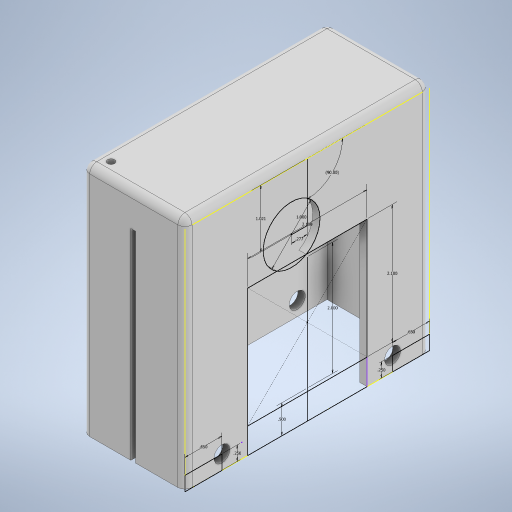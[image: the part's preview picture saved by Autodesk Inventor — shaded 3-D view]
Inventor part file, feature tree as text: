
AUTODESK INVENTOR PART (.ipt)
format: ipt  version: 2024.1 (Build 281209000, 209)  size: 335,872 bytes
history: native  units: in
note: dims shown in document units (in); Inventor stores cm internally (conversion verified against a paired STEP export)
features: extrude x6, sketch x6, hole x2, fillet x1
ambient origin geometry x8: Origin, YZ Plane, XZ Plane, XY Plane, X Axis, Y Axis, Z Axis, Center Point
bodies: Solid1 (feature_tree)
feature tree (15):
  extrude  "Extrusion1"  Depth=4.0in
  sketch  "Sketch2"  dims[d2=0.25in d3=0.25in]
  extrude  "Extrusion2"  Depth=0.25in
  hole  "Hole1"  [1 undecoded]
  extrude  "Extrusion3"  Depth=4.3in
  fillet  "Fillet1"  Radius=4.0in
  extrude  "Extrusion4"  Depth=0.25in
  hole  "Hole2"  [1 undecoded]
  extrude  "Extrusion5"  Depth=2.1in
  extrude  "Extrusion6"  Depth=2.1in
  sketch  "Sketch1"  dims[d0=1.0in d1=4.0in]
  sketch  "Sketch3"  dims[d4=1.55in d5=4.05in]
  sketch  "Sketch4"  dims[d6=1.8in d7=4.3in d8=4.0in d9=0.0in]
  sketch  "Sketch5"  dims[d12=0.65in d13=0.25in]
  sketch  "Sketch6"  dims[d14=0.5in d15=2.0in d16=2.1in d17=2.1in d18=0.125in d19=0.0in d20=0.281in d21=0.75in d22=0.438in d23=0.25in d24=0.5635in d25=1.0in d26=0.8108in d27=0.125in d28=0.0in d29=0.125in d30=1.021in d31=90.0deg d33=0.0in d34=0.0in d37=0.277in d38=1.0in d39=0.125in d40=0.125in d41=0.125in d42=0.75in d43=0.375in d44=0.25in d45=0.5635in d46=1.0in d47=0.8108in d48=0.65in d49=0.25in d50=0.775in d51=0.325in d52=0.325in d53=0.25in d54=0.0in d55=0.5in d56=0.0312in d57=0.0312in d58=0.0825in d59=3.6in d60=0.25in d61=0.0in d62=0.0312in d63=0.0312in d64=0.0625in d65=3.6in]
note: 2 required parameter values undecoded (feature->parameter linkage not recoverable at this tier; creation-order binding heuristic only, values carry confidence <= 0.55)
